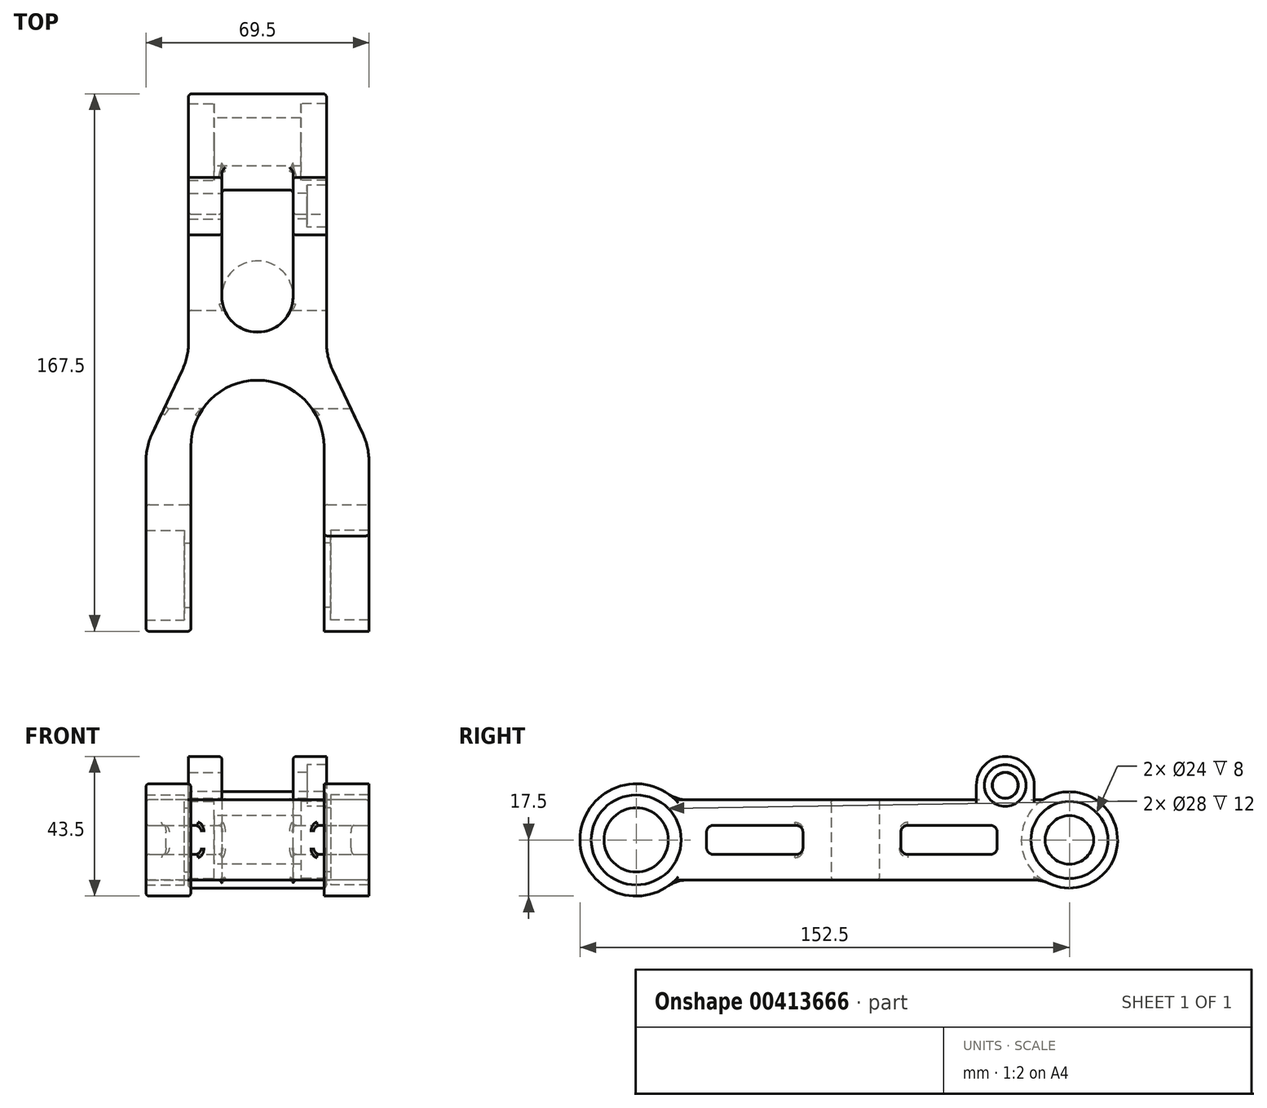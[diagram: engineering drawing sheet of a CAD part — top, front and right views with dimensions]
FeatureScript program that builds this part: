
annotation { "Feature Type Name" : "Feature", "Feature Type Description" : "" }
export const myFeature = defineFeature(function(context is Context, id is Id, definition is map)
    precondition{}
    {
        {
            var Q0;
            Q0=qCreatedBy(makeId("Top.planeOp"),FACE);
            var sketch = newSketch(context, id + "F0", { "sketchPlane" : qUnion([Q0])});
            skLineSegment(sketch, "E0", {"start": v(-21.5, 135) * mm, "end": v(-21.5, 68) * mm});
            skLineSegment(sketch, "E1", {"start": v(-21.5, 68) * mm, "end": v(-34.75, 40) * mm});
            skLineSegment(sketch, "E2", {"start": v(-34.75, 40) * mm, "end": v(-34.75, 0) * mm});
            skLineSegment(sketch, "E3", {"start": v(-34.75, 0) * mm, "end": v(-20.75, 0) * mm});
            skLineSegment(sketch, "E4", {"start": v(-20.75, 0) * mm, "end": v(-20.75, 40) * mm});
            skLineSegment(sketch, "E5", {"start": v(20.75, 0) * mm, "end": v(20.75, 40) * mm});
            skLineSegment(sketch, "E6", {"start": v(20.75, 0) * mm, "end": v(34.75, 0) * mm});
            skLineSegment(sketch, "E7", {"start": v(34.75, 0) * mm, "end": v(34.75, 40) * mm});
            skLineSegment(sketch, "E8", {"start": v(34.75, 40) * mm, "end": v(21.5, 68) * mm});
            skLineSegment(sketch, "E9", {"start": v(21.5, 68) * mm, "end": v(21.5, 135) * mm});
            skLineSegment(sketch, "E10", {"start": v(11.1, 135) * mm, "end": v(21.5, 135) * mm});
            skLineSegment(sketch, "E11", {"start": v(0, 0) * mm, "end": v(0, 68) * mm, "construction": true});
            skLineSegment(sketch, "E12", {"start": v(-11.1, 135) * mm, "end": v(-11.1, 86.85) * mm});
            skLineSegment(sketch, "E13", {"start": v(11.1, 86.85) * mm, "end": v(11.1, 135) * mm});
            skPoint(sketch, "E14.orphan", {"position": v(0, 135) * mm});
            skLineSegment(sketch, "E15", {"start": v(-34.75, 40) * mm, "end": v(34.75, 40) * mm, "construction": true});
            skArc(sketch, "E16", {"start": v(20.75, 40) * mm, "mid": v(0, 60.75) * mm, "end": v(-20.75, 40) * mm});
            skLineSegment(sketch, "E17", {"start": v(-21.5, 135) * mm, "end": v(-11.1, 135) * mm});
            skArc(sketch, "E18", {"start": v(-11.1, 86.85) * mm, "mid": v(0, 75.75) * mm, "end": v(11.1, 86.85) * mm});
            skLineSegment(sketch, "E19", {"start": v(-21.5, 68) * mm, "end": v(21.5, 68) * mm, "construction": true});
            skSolve(sketch);
        }
        {
            var Q0;
            Q0=makeQuery(id+"F0.imprint","IMPRINT",FACE,{"disambiguationData":[TD([[makeQuery(id+"F0.imprint","IMPRINT",EDGE,{"derivedFrom":sQuery(id+"F0.wireOp",EDGE,"E0")}),1.0]])]});
            extrude(context, id + "F1", {"entities" : qUnion([Q0]), "depth" : 25 * mm, "offsetDistance" : 25 * mm, "symmetric" : true});
        }
        {
            var Q0;
            Q0=makeQuery(id+"F1.opExtrude","SWEPT_FACE",FACE,{"disambiguationData":[OSD([sQuery(id+"F0.wireOp",EDGE,"E0")])]});
            var sketch = newSketch(context, id + "F2", { "sketchPlane" : qUnion([Q0])});
            skCircle(sketch, "E20", {"center": v(-135, 0) * mm, "radius": 15 * mm});
            skSolve(sketch);
        }
        {
            var Q0;
            Q0 = qSketchRegion(id + "F2", true);
            var Q1;
            Q1=makeQuery(id+"F1.opExtrude","SWEPT_FACE",FACE,{"disambiguationData":[OSD([sQuery(id+"F0.wireOp",EDGE,"E9")])]});
            extrude(context, id + "F3", {"entities" : qUnion([Q0]), "operationType" : NewBodyOperationType.ADD, "endBound" : BoundingType.UP_TO_SURFACE, "oppositeDirection" : true, "endBoundEntityFace" : qUnion([Q1]), "depth" : 25 * mm});
        }
        {
            var Q0;
            Q0=makeQuery(id+"F1.opExtrude","SWEPT_FACE",FACE,{"disambiguationData":[OSD([sQuery(id+"F0.wireOp",EDGE,"E4")])]});
            var sketch = newSketch(context, id + "F4", { "sketchPlane" : qUnion([Q0])});
            skCircle(sketch, "E21", {"center": v(0, 0) * mm, "radius": 17.5 * mm});
            skSolve(sketch);
        }
        {
            var Q0;
            Q0 = qSketchRegion(id + "F4", true);
            var Q1;
            Q1=makeQuery(id+"F1.opExtrude","SWEPT_FACE",FACE,{"disambiguationData":[OSD([sQuery(id+"F0.wireOp",EDGE,"E2")])]});
            extrude(context, id + "F5", {"entities" : qUnion([Q0]), "operationType" : NewBodyOperationType.ADD, "endBound" : BoundingType.UP_TO_SURFACE, "oppositeDirection" : true, "endBoundEntityFace" : qUnion([Q1]), "depth" : 25 * mm});
        }
        {
            var Q0;
            Q0=makeQuery(id+"F1.opExtrude","SWEPT_FACE",FACE,{"disambiguationData":[OSD([sQuery(id+"F0.wireOp",EDGE,"E5")])]});
            var sketch = newSketch(context, id + "F6", { "sketchPlane" : qUnion([Q0])});
            skCircle(sketch, "E22", {"center": v(0, 0) * mm, "radius": 17.5 * mm});
            skSolve(sketch);
        }
        {
            var Q0;
            {var subQ1=sQuery(id+"F0.wireOp",EDGE,"E5");var subQ6=makeQuery(id+"F1.opExtrude","SWEPT_EDGE",EDGE,{"disambiguationData":[OSD([subQ1,sQuery(id+"F0.wireOp",EDGE,"E6")])]});Q0=makeQuery(id+"F6.imprint","IMPRINT",FACE,{"disambiguationData":[TD([[makeQuery(id+"F6.imprint","IMPRINT",EDGE,{"derivedFrom":subQ6}),1.0]])]});}
            var Q1;
            Q1=makeQuery(id+"F1.opExtrude","SWEPT_FACE",FACE,{"disambiguationData":[OSD([sQuery(id+"F0.wireOp",EDGE,"E7")])]});
            extrude(context, id + "F7", {"entities" : qUnion([Q0]), "operationType" : NewBodyOperationType.ADD, "endBound" : BoundingType.UP_TO_SURFACE, "oppositeDirection" : true, "endBoundEntityFace" : qUnion([Q1]), "depth" : 25 * mm});
        }
        {
            var Q0;
            Q0=qCreatedBy(makeId("Right.planeOp"),FACE);
            var sketch = newSketch(context, id + "F8", { "sketchPlane" : qUnion([Q0])});
            skArc(sketch, "E23", {"start": v(124, 17) * mm, "mid": v(115, 26) * mm, "end": v(106, 17) * mm});
            skLineSegment(sketch, "E24", {"start": v(106, 17) * mm, "end": v(106, 12.5) * mm});
            skLineSegment(sketch, "E25", {"start": v(124, 17) * mm, "end": v(124, 12.5) * mm});
            skLineSegment(sketch, "E26", {"start": v(106, 17) * mm, "end": v(124, 17) * mm, "construction": true});
            skLineSegment(sketch, "E27", {"start": v(106, 12.5) * mm, "end": v(124, 12.5) * mm});
            skSolve(sketch);
        }
        {
            var Q0;
            Q0=makeQuery(id+"F8.imprint","IMPRINT",FACE,{"disambiguationData":[TD([[makeQuery(id+"F8.imprint","IMPRINT",EDGE,{"derivedFrom":sQuery(id+"F8.wireOp",EDGE,"E23")}),1.0]])]});
            var Q1;
            Q1=sQuery(id+"F8.wireOp",EDGE,"E23");
            var Q2;
            Q2=makeQuery(id+"F3.boolean.opBoolean","MERGE",FACE,{"derivedFrom":[makeQuery(id+"F1.opExtrude","SWEPT_FACE",FACE,{"disambiguationData":[OSD([sQuery(id+"F0.wireOp",EDGE,"E9")])]}),makeQuery(id+"F3.opExtrude","CAP_FACE",FACE,{"disambiguationData":[OSD([sQuery(id+"F2.wireOp",EDGE,"E20")])],"isStart":false})]});
            var Q3;
            Q3=makeQuery(id+"F1.opExtrude","SWEPT_FACE",FACE,{"disambiguationData":[OSD([sQuery(id+"F0.wireOp",EDGE,"E13")])]});
            extrude(context, id + "F9", {"entities" : qUnion([Q0]), "operationType" : NewBodyOperationType.ADD, "surfaceEntities" : qUnion([Q1]), "endBound" : BoundingType.UP_TO_SURFACE, "endBoundEntityFace" : qUnion([Q2]), "depth" : 45 * mm, "hasSecondDirection" : true, "secondDirectionBound" : BoundingType.UP_TO_SURFACE, "secondDirectionOppositeDirection" : false, "secondDirectionBoundEntityFace" : qUnion([Q3]), "secondDirectionDepth" : (45 / 2) * mm});
        }
        {
            var Q0;
            Q0 = qSketchRegion(id + "F8", true);
            var Q1;
            Q1=makeQuery(id+"F3.boolean.opBoolean","MERGE",FACE,{"derivedFrom":[makeQuery(id+"F1.opExtrude","SWEPT_FACE",FACE,{"disambiguationData":[OSD([sQuery(id+"F0.wireOp",EDGE,"E0")])]}),makeQuery(id+"F3.opExtrude","CAP_FACE",FACE,{"disambiguationData":[OSD([sQuery(id+"F2.wireOp",EDGE,"E20")])],"isStart":true})]});
            var Q2;
            Q2=makeQuery(id+"F1.opExtrude","SWEPT_FACE",FACE,{"disambiguationData":[OSD([sQuery(id+"F0.wireOp",EDGE,"E12")])]});
            extrude(context, id + "F10", {"entities" : qUnion([Q0]), "operationType" : NewBodyOperationType.ADD, "endBound" : BoundingType.UP_TO_SURFACE, "oppositeDirection" : true, "endBoundEntityFace" : qUnion([Q1]), "depth" : 25 * mm, "hasSecondDirection" : true, "secondDirectionBound" : BoundingType.UP_TO_SURFACE, "secondDirectionOppositeDirection" : true, "secondDirectionBoundEntityFace" : qUnion([Q2]), "secondDirectionDepth" : 25 * mm});
        }
        {
            var Q0;
            Q0=makeQuery(id+"F1.opExtrude","SWEPT_EDGE",EDGE,{"disambiguationData":[OSD([sQuery(id+"F0.wireOp",EDGE,"E0"),sQuery(id+"F0.wireOp",EDGE,"E1")])]});
            var Q1;
            Q1=makeQuery(id+"F1.opExtrude","SWEPT_EDGE",EDGE,{"disambiguationData":[OSD([sQuery(id+"F0.wireOp",EDGE,"E1"),sQuery(id+"F0.wireOp",EDGE,"E2")])]});
            var Q2;
            Q2=makeQuery(id+"F1.opExtrude","SWEPT_EDGE",EDGE,{"disambiguationData":[OSD([sQuery(id+"F0.wireOp",EDGE,"E8"),sQuery(id+"F0.wireOp",EDGE,"E9")])]});
            var Q3;
            Q3=makeQuery(id+"F1.opExtrude","SWEPT_EDGE",EDGE,{"disambiguationData":[OSD([sQuery(id+"F0.wireOp",EDGE,"E7"),sQuery(id+"F0.wireOp",EDGE,"E8")])]});
            fillet(context, id + "F11", {"entities" : qUnion([Q0, Q1, Q2, Q3]), "radius" : 20 * mm, "tangentPropagation" : true, "allowEdgeOverflow" : false});
        }
        {
            var Q0;
            Q0=makeQuery(id+"F9.opExtrude","TWEAK_EDGE",EDGE,{"derivedFrom":[makeQuery(id+"F8.imprint","IMPRINT",EDGE,{"derivedFrom":sQuery(id+"F8.wireOp",EDGE,"E24")}),makeQuery(id+"F8.imprint","IMPRINT",EDGE,{"derivedFrom":sQuery(id+"F8.wireOp",EDGE,"E27")})]});
            var Q1;
            Q1=makeQuery(id+"F10.opExtrude","TWEAK_EDGE",EDGE,{"derivedFrom":[makeQuery(id+"F8.imprint","IMPRINT",EDGE,{"derivedFrom":sQuery(id+"F8.wireOp",EDGE,"E24")}),makeQuery(id+"F8.imprint","IMPRINT",EDGE,{"derivedFrom":sQuery(id+"F8.wireOp",EDGE,"E27")})]});
            var Q2;
            Q2=makeQuery(id+"F9.boolean.opBoolean","INTERSECT",EDGE,{"derivedFrom":[makeQuery(id+"F3.opExtrude","SWEPT_FACE",FACE,{"disambiguationData":[OSD([sQuery(id+"F2.wireOp",EDGE,"E20")])]}),makeQuery(id+"F9.opExtrude","SWEPT_FACE",FACE,{"disambiguationData":[OSD([sQuery(id+"F8.wireOp",EDGE,"E25")])]})]});
            var Q3;
            Q3=makeQuery(id+"F10.boolean.opBoolean","INTERSECT",EDGE,{"derivedFrom":[makeQuery(id+"F3.opExtrude","SWEPT_FACE",FACE,{"disambiguationData":[OSD([sQuery(id+"F2.wireOp",EDGE,"E20")])]}),makeQuery(id+"F10.opExtrude","SWEPT_FACE",FACE,{"disambiguationData":[OSD([sQuery(id+"F8.wireOp",EDGE,"E25")])]})]});
            var Q4;
            {var subQ0=sQuery(id+"F6.wireOp",EDGE,"E22");var subQ1=sQuery(id+"F0.wireOp",EDGE,"E5");Q4=makeQuery(id+"F7.opExtrude","SWEPT_EDGE",EDGE,{"disambiguationData":[OSD([subQ1,subQ0]),TDD([makeQuery(id+"F6.imprint","INTERSECT",VERTEX,{"derivedFrom":[makeQuery(id+"F1.opExtrude","CAP_EDGE",EDGE,{"disambiguationData":[OSD([subQ1])],"isStart":false}),subQ0]})])]});}
            var Q5;
            Q5=makeQuery(id+"F5.boolean.opBoolean","INTERSECT",EDGE,{"derivedFrom":[makeQuery(id+"F1.opExtrude","CAP_FACE",FACE,{"disambiguationData":[OSD([sQuery(id+"F0.wireOp",EDGE,"E0"),sQuery(id+"F0.wireOp",EDGE,"E1"),sQuery(id+"F0.wireOp",EDGE,"E2"),sQuery(id+"F0.wireOp",EDGE,"E3"),sQuery(id+"F0.wireOp",EDGE,"E4"),sQuery(id+"F0.wireOp",EDGE,"E5"),sQuery(id+"F0.wireOp",EDGE,"E6"),sQuery(id+"F0.wireOp",EDGE,"E7"),sQuery(id+"F0.wireOp",EDGE,"E8"),sQuery(id+"F0.wireOp",EDGE,"E9"),sQuery(id+"F0.wireOp",EDGE,"E10"),sQuery(id+"F0.wireOp",EDGE,"E12"),sQuery(id+"F0.wireOp",EDGE,"E13"),sQuery(id+"F0.wireOp",EDGE,"E16"),sQuery(id+"F0.wireOp",EDGE,"E17"),sQuery(id+"F0.wireOp",EDGE,"E18")])],"isStart":false}),makeQuery(id+"F5.opExtrude","SWEPT_FACE",FACE,{"disambiguationData":[OSD([sQuery(id+"F4.wireOp",EDGE,"E21")])]})]});
            var Q6;
            {var subQ0=sQuery(id+"F6.wireOp",EDGE,"E22");var subQ1=sQuery(id+"F0.wireOp",EDGE,"E5");Q6=makeQuery(id+"F7.opExtrude","SWEPT_EDGE",EDGE,{"disambiguationData":[OSD([subQ1,subQ0]),TDD([makeQuery(id+"F6.imprint","INTERSECT",VERTEX,{"derivedFrom":[makeQuery(id+"F1.opExtrude","CAP_EDGE",EDGE,{"disambiguationData":[OSD([subQ1])],"isStart":true}),subQ0]})])]});}
            var Q7;
            Q7=makeQuery(id+"F5.boolean.opBoolean","INTERSECT",EDGE,{"derivedFrom":[makeQuery(id+"F1.opExtrude","CAP_FACE",FACE,{"disambiguationData":[OSD([sQuery(id+"F0.wireOp",EDGE,"E0"),sQuery(id+"F0.wireOp",EDGE,"E1"),sQuery(id+"F0.wireOp",EDGE,"E2"),sQuery(id+"F0.wireOp",EDGE,"E3"),sQuery(id+"F0.wireOp",EDGE,"E4"),sQuery(id+"F0.wireOp",EDGE,"E5"),sQuery(id+"F0.wireOp",EDGE,"E6"),sQuery(id+"F0.wireOp",EDGE,"E7"),sQuery(id+"F0.wireOp",EDGE,"E8"),sQuery(id+"F0.wireOp",EDGE,"E9"),sQuery(id+"F0.wireOp",EDGE,"E10"),sQuery(id+"F0.wireOp",EDGE,"E12"),sQuery(id+"F0.wireOp",EDGE,"E13"),sQuery(id+"F0.wireOp",EDGE,"E16"),sQuery(id+"F0.wireOp",EDGE,"E17"),sQuery(id+"F0.wireOp",EDGE,"E18")])],"isStart":true}),makeQuery(id+"F5.opExtrude","SWEPT_FACE",FACE,{"disambiguationData":[OSD([sQuery(id+"F4.wireOp",EDGE,"E21")])]})]});
            var Q8;
            Q8=makeQuery(id+"F3.boolean.opBoolean","INTERSECT",EDGE,{"disambiguationData":[OD(1.0)],"derivedFrom":[makeQuery(id+"F1.opExtrude","CAP_FACE",FACE,{"disambiguationData":[OSD([sQuery(id+"F0.wireOp",EDGE,"E0"),sQuery(id+"F0.wireOp",EDGE,"E1"),sQuery(id+"F0.wireOp",EDGE,"E2"),sQuery(id+"F0.wireOp",EDGE,"E3"),sQuery(id+"F0.wireOp",EDGE,"E4"),sQuery(id+"F0.wireOp",EDGE,"E5"),sQuery(id+"F0.wireOp",EDGE,"E6"),sQuery(id+"F0.wireOp",EDGE,"E7"),sQuery(id+"F0.wireOp",EDGE,"E8"),sQuery(id+"F0.wireOp",EDGE,"E9"),sQuery(id+"F0.wireOp",EDGE,"E10"),sQuery(id+"F0.wireOp",EDGE,"E12"),sQuery(id+"F0.wireOp",EDGE,"E13"),sQuery(id+"F0.wireOp",EDGE,"E16"),sQuery(id+"F0.wireOp",EDGE,"E17"),sQuery(id+"F0.wireOp",EDGE,"E18")])],"isStart":true}),makeQuery(id+"F3.opExtrude","SWEPT_FACE",FACE,{"disambiguationData":[OSD([sQuery(id+"F2.wireOp",EDGE,"E20")])]})]});
            var Q9;
            Q9=makeQuery(id+"F3.boolean.opBoolean","INTERSECT",EDGE,{"disambiguationData":[OD(0.0)],"derivedFrom":[makeQuery(id+"F1.opExtrude","CAP_FACE",FACE,{"disambiguationData":[OSD([sQuery(id+"F0.wireOp",EDGE,"E0"),sQuery(id+"F0.wireOp",EDGE,"E1"),sQuery(id+"F0.wireOp",EDGE,"E2"),sQuery(id+"F0.wireOp",EDGE,"E3"),sQuery(id+"F0.wireOp",EDGE,"E4"),sQuery(id+"F0.wireOp",EDGE,"E5"),sQuery(id+"F0.wireOp",EDGE,"E6"),sQuery(id+"F0.wireOp",EDGE,"E7"),sQuery(id+"F0.wireOp",EDGE,"E8"),sQuery(id+"F0.wireOp",EDGE,"E9"),sQuery(id+"F0.wireOp",EDGE,"E10"),sQuery(id+"F0.wireOp",EDGE,"E12"),sQuery(id+"F0.wireOp",EDGE,"E13"),sQuery(id+"F0.wireOp",EDGE,"E16"),sQuery(id+"F0.wireOp",EDGE,"E17"),sQuery(id+"F0.wireOp",EDGE,"E18")])],"isStart":true}),makeQuery(id+"F3.opExtrude","SWEPT_FACE",FACE,{"disambiguationData":[OSD([sQuery(id+"F2.wireOp",EDGE,"E20")])]})]});
            fillet(context, id + "F12", {"entities" : qUnion([Q0, Q1, Q2, Q3, Q4, Q5, Q6, Q7, Q8, Q9]), "radius" : 10 * mm, "allowEdgeOverflow" : false});
        }
        {
            var Q0;
            Q0=makeQuery(id+"F3.boolean.opBoolean","INTERSECT",EDGE,{"disambiguationData":[OD(1.0)],"derivedFrom":[makeQuery(id+"F1.opExtrude","CAP_FACE",FACE,{"disambiguationData":[OSD([sQuery(id+"F0.wireOp",EDGE,"E0"),sQuery(id+"F0.wireOp",EDGE,"E1"),sQuery(id+"F0.wireOp",EDGE,"E2"),sQuery(id+"F0.wireOp",EDGE,"E3"),sQuery(id+"F0.wireOp",EDGE,"E4"),sQuery(id+"F0.wireOp",EDGE,"E5"),sQuery(id+"F0.wireOp",EDGE,"E6"),sQuery(id+"F0.wireOp",EDGE,"E7"),sQuery(id+"F0.wireOp",EDGE,"E8"),sQuery(id+"F0.wireOp",EDGE,"E9"),sQuery(id+"F0.wireOp",EDGE,"E10"),sQuery(id+"F0.wireOp",EDGE,"E12"),sQuery(id+"F0.wireOp",EDGE,"E13"),sQuery(id+"F0.wireOp",EDGE,"E16"),sQuery(id+"F0.wireOp",EDGE,"E17"),sQuery(id+"F0.wireOp",EDGE,"E18")])],"isStart":false}),makeQuery(id+"F3.opExtrude","SWEPT_FACE",FACE,{"disambiguationData":[OSD([sQuery(id+"F2.wireOp",EDGE,"E20")])]})]});
            var Q1;
            Q1=makeQuery(id+"F9.opExtrude","TWEAK_EDGE",EDGE,{"derivedFrom":[makeQuery(id+"F8.imprint","IMPRINT",EDGE,{"derivedFrom":sQuery(id+"F8.wireOp",EDGE,"E25")}),makeQuery(id+"F8.imprint","IMPRINT",EDGE,{"derivedFrom":sQuery(id+"F8.wireOp",EDGE,"E27")})]});
            var Q2;
            Q2=makeQuery(id+"F10.opExtrude","TWEAK_EDGE",EDGE,{"derivedFrom":[makeQuery(id+"F8.imprint","IMPRINT",EDGE,{"derivedFrom":sQuery(id+"F8.wireOp",EDGE,"E25")}),makeQuery(id+"F8.imprint","IMPRINT",EDGE,{"derivedFrom":sQuery(id+"F8.wireOp",EDGE,"E27")})]});
            var Q3;
            Q3=makeQuery(id+"F3.boolean.opBoolean","INTERSECT",EDGE,{"disambiguationData":[OD(0.0)],"derivedFrom":[makeQuery(id+"F1.opExtrude","CAP_FACE",FACE,{"disambiguationData":[OSD([sQuery(id+"F0.wireOp",EDGE,"E0"),sQuery(id+"F0.wireOp",EDGE,"E1"),sQuery(id+"F0.wireOp",EDGE,"E2"),sQuery(id+"F0.wireOp",EDGE,"E3"),sQuery(id+"F0.wireOp",EDGE,"E4"),sQuery(id+"F0.wireOp",EDGE,"E5"),sQuery(id+"F0.wireOp",EDGE,"E6"),sQuery(id+"F0.wireOp",EDGE,"E7"),sQuery(id+"F0.wireOp",EDGE,"E8"),sQuery(id+"F0.wireOp",EDGE,"E9"),sQuery(id+"F0.wireOp",EDGE,"E10"),sQuery(id+"F0.wireOp",EDGE,"E12"),sQuery(id+"F0.wireOp",EDGE,"E13"),sQuery(id+"F0.wireOp",EDGE,"E16"),sQuery(id+"F0.wireOp",EDGE,"E17"),sQuery(id+"F0.wireOp",EDGE,"E18")])],"isStart":false}),makeQuery(id+"F3.opExtrude","SWEPT_FACE",FACE,{"disambiguationData":[OSD([sQuery(id+"F2.wireOp",EDGE,"E20")])]})]});
            var Q4;
            Q4=makeQuery(id+"F3.boolean.opBoolean","INTERSECT",EDGE,{"derivedFrom":[makeQuery(id+"F1.opExtrude","SWEPT_FACE",FACE,{"disambiguationData":[OSD([sQuery(id+"F0.wireOp",EDGE,"E13")])]}),makeQuery(id+"F3.opExtrude","SWEPT_FACE",FACE,{"disambiguationData":[OSD([sQuery(id+"F2.wireOp",EDGE,"E20")])]})]});
            var Q5;
            Q5=makeQuery(id+"F3.boolean.opBoolean","INTERSECT",EDGE,{"derivedFrom":[makeQuery(id+"F1.opExtrude","SWEPT_FACE",FACE,{"disambiguationData":[OSD([sQuery(id+"F0.wireOp",EDGE,"E12")])]}),makeQuery(id+"F3.opExtrude","SWEPT_FACE",FACE,{"disambiguationData":[OSD([sQuery(id+"F2.wireOp",EDGE,"E20")])]})]});
            fillet(context, id + "F13", {"entities" : qUnion([Q0, Q1, Q2, Q3, Q4, Q5]), "radius" : 1 * mm, "tangentPropagation" : true, "allowEdgeOverflow" : false});
        }
        {
            var Q0;
            Q0=makeQuery(id+"F10.opExtrude","CAP_EDGE",EDGE,{"disambiguationData":[OSD([sQuery(id+"F8.wireOp",EDGE,"E23")])],"isStart":true});
            var Q1;
            Q1=makeQuery(id+"F9.opExtrude","CAP_EDGE",EDGE,{"disambiguationData":[OSD([sQuery(id+"F8.wireOp",EDGE,"E23")])],"isStart":true});
            fillet(context, id + "F14", {"entities" : qUnion([Q0, Q1]), "radius" : 1 * mm, "tangentPropagation" : true, "allowEdgeOverflow" : false});
        }
        {
            var Q0;
            Q0=makeQuery(id+"F1.opExtrude","CAP_EDGE",EDGE,{"disambiguationData":[OSD([sQuery(id+"F0.wireOp",EDGE,"E13")])],"isStart":true});
            var Q1;
            Q1=makeQuery(id+"F1.opExtrude","CAP_EDGE",EDGE,{"disambiguationData":[OSD([sQuery(id+"F0.wireOp",EDGE,"E12")])],"isStart":true});
            fillet(context, id + "F15", {"entities" : qUnion([Q0, Q1]), "radius" : 1 * mm, "tangentPropagation" : true, "allowEdgeOverflow" : false});
        }
        {
            var Q0;
            Q0=makeQuery(id+"F1.opExtrude","CAP_EDGE",EDGE,{"disambiguationData":[OSD([sQuery(id+"F0.wireOp",EDGE,"E5")])],"isStart":true});
            fillet(context, id + "F16", {"entities" : qUnion([Q0]), "radius" : 1 * mm, "tangentPropagation" : true, "allowEdgeOverflow" : false});
        }
        {
            var Q0;
            Q0=makeQuery(id+"F1.opExtrude","CAP_EDGE",EDGE,{"disambiguationData":[OSD([sQuery(id+"F0.wireOp",EDGE,"E9")])],"isStart":false});
            var Q1;
            Q1=makeQuery(id+"F1.opExtrude","CAP_EDGE",EDGE,{"disambiguationData":[OSD([sQuery(id+"F0.wireOp",EDGE,"E0")])],"isStart":false});
            fillet(context, id + "F17", {"entities" : qUnion([Q0, Q1]), "radius" : 1 * mm, "tangentPropagation" : true, "allowEdgeOverflow" : false});
        }
        {
            var Q0;
            Q0=makeQuery(id+"F9.boolean.opBoolean","MERGE",FACE,{"derivedFrom":[makeQuery(id+"F3.boolean.opBoolean","MERGE",FACE,{"derivedFrom":[makeQuery(id+"F1.opExtrude","SWEPT_FACE",FACE,{"disambiguationData":[OSD([sQuery(id+"F0.wireOp",EDGE,"E9")])]}),makeQuery(id+"F3.opExtrude","CAP_FACE",FACE,{"disambiguationData":[OSD([sQuery(id+"F2.wireOp",EDGE,"E20")])],"isStart":false})]}),makeQuery(id+"F9.opExtrude","CAP_FACE",FACE,{"disambiguationData":[OSD([sQuery(id+"F8.wireOp",EDGE,"E23"),sQuery(id+"F8.wireOp",EDGE,"E24"),sQuery(id+"F8.wireOp",EDGE,"E25"),sQuery(id+"F8.wireOp",EDGE,"E27")])],"isStart":false})]});
            var sketch = newSketch(context, id + "F18", { "sketchPlane" : qUnion([Q0])});
            skPoint(sketch, "E28", {"position": v(115, 17) * mm});
            skSolve(sketch);
        }
        {
            var Q0;
            Q0=sQuery(id+"F18.wireOp",VERTEX,"E28");
            var Q1;
            Q1=makeQuery(id+"F1.opExtrude","SWEPT_BODY",BODY,{"disambiguationData":[OSD([sQuery(id+"F0.wireOp",EDGE,"E0"),sQuery(id+"F0.wireOp",EDGE,"E1"),sQuery(id+"F0.wireOp",EDGE,"E2"),sQuery(id+"F0.wireOp",EDGE,"E3"),sQuery(id+"F0.wireOp",EDGE,"E4"),sQuery(id+"F0.wireOp",EDGE,"E5"),sQuery(id+"F0.wireOp",EDGE,"E6"),sQuery(id+"F0.wireOp",EDGE,"E7"),sQuery(id+"F0.wireOp",EDGE,"E8"),sQuery(id+"F0.wireOp",EDGE,"E9"),sQuery(id+"F0.wireOp",EDGE,"E10"),sQuery(id+"F0.wireOp",EDGE,"E12"),sQuery(id+"F0.wireOp",EDGE,"E13"),sQuery(id+"F0.wireOp",EDGE,"E16"),sQuery(id+"F0.wireOp",EDGE,"E17"),sQuery(id+"F0.wireOp",EDGE,"E18")])]});
            hole(context, id + "F19", {"style" : HoleStyle.C_BORE, "endStyle" : HoleEndStyle.BLIND, "holeDiameter" : 8.1 * mm, "cBoreDiameter" : 13 * mm, "cBoreDepth" : 6 * mm, "majorDiameter" : 5 * mm, "holeDepth" : 12 * mm, "isTappedThrough" : true, "tappedDepth" : 12 * mm, "tapClearance" : 3, "locations" : qUnion([Q0]), "scope" : qUnion([Q1]), "startStyle" : HoleStartStyle.SKETCH});
        }
        {
            var Q0;
            Q0=makeQuery(id+"F10.boolean.opBoolean","MERGE",FACE,{"derivedFrom":[makeQuery(id+"F3.boolean.opBoolean","MERGE",FACE,{"derivedFrom":[makeQuery(id+"F1.opExtrude","SWEPT_FACE",FACE,{"disambiguationData":[OSD([sQuery(id+"F0.wireOp",EDGE,"E0")])]}),makeQuery(id+"F3.opExtrude","CAP_FACE",FACE,{"disambiguationData":[OSD([sQuery(id+"F2.wireOp",EDGE,"E20")])],"isStart":true})]}),makeQuery(id+"F10.opExtrude","CAP_FACE",FACE,{"disambiguationData":[OSD([sQuery(id+"F8.wireOp",EDGE,"E23"),sQuery(id+"F8.wireOp",EDGE,"E24"),sQuery(id+"F8.wireOp",EDGE,"E25"),sQuery(id+"F8.wireOp",EDGE,"E27")])],"isStart":false})]});
            var sketch = newSketch(context, id + "F20", { "sketchPlane" : qUnion([Q0])});
            skPoint(sketch, "E29", {"position": v(-115, 17) * mm});
            skSolve(sketch);
        }
        {
            var Q0;
            Q0=sQuery(id+"F20.wireOp",VERTEX,"E29");
            var Q1;
            Q1=makeQuery(id+"F1.opExtrude","SWEPT_BODY",BODY,{"disambiguationData":[OSD([sQuery(id+"F0.wireOp",EDGE,"E0"),sQuery(id+"F0.wireOp",EDGE,"E1"),sQuery(id+"F0.wireOp",EDGE,"E2"),sQuery(id+"F0.wireOp",EDGE,"E3"),sQuery(id+"F0.wireOp",EDGE,"E4"),sQuery(id+"F0.wireOp",EDGE,"E5"),sQuery(id+"F0.wireOp",EDGE,"E6"),sQuery(id+"F0.wireOp",EDGE,"E7"),sQuery(id+"F0.wireOp",EDGE,"E8"),sQuery(id+"F0.wireOp",EDGE,"E9"),sQuery(id+"F0.wireOp",EDGE,"E10"),sQuery(id+"F0.wireOp",EDGE,"E12"),sQuery(id+"F0.wireOp",EDGE,"E13"),sQuery(id+"F0.wireOp",EDGE,"E16"),sQuery(id+"F0.wireOp",EDGE,"E17"),sQuery(id+"F0.wireOp",EDGE,"E18")])]});
            hole(context, id + "F21", {"style" : HoleStyle.SIMPLE, "endStyle" : HoleEndStyle.BLIND, "holeDiameter" : 8 * mm, "holeDepth" : 15.75 * mm, "isTappedThrough" : true, "tappedDepth" : 12 * mm, "tapClearance" : 3, "locations" : qUnion([Q0]), "scope" : qUnion([Q1]), "startStyle" : HoleStartStyle.SKETCH});
        }
        {
            var Q0;
            Q0=makeQuery(id+"F9.boolean.opBoolean","MERGE",FACE,{"derivedFrom":[makeQuery(id+"F3.boolean.opBoolean","MERGE",FACE,{"derivedFrom":[makeQuery(id+"F1.opExtrude","SWEPT_FACE",FACE,{"disambiguationData":[OSD([sQuery(id+"F0.wireOp",EDGE,"E9")])]}),makeQuery(id+"F3.opExtrude","CAP_FACE",FACE,{"disambiguationData":[OSD([sQuery(id+"F2.wireOp",EDGE,"E20")])],"isStart":false})]}),makeQuery(id+"F9.opExtrude","CAP_FACE",FACE,{"disambiguationData":[OSD([sQuery(id+"F8.wireOp",EDGE,"E23"),sQuery(id+"F8.wireOp",EDGE,"E24"),sQuery(id+"F8.wireOp",EDGE,"E25"),sQuery(id+"F8.wireOp",EDGE,"E27")])],"isStart":false})]});
            var sketch = newSketch(context, id + "F22", { "sketchPlane" : qUnion([Q0])});
            skPoint(sketch, "E30", {"position": v(135, 0) * mm});
            skSolve(sketch);
        }
        {
            var Q0;
            Q0=sQuery(id+"F22.wireOp",VERTEX,"E30");
            var Q1;
            Q1=makeQuery(id+"F1.opExtrude","SWEPT_BODY",BODY,{"disambiguationData":[OSD([sQuery(id+"F0.wireOp",EDGE,"E0"),sQuery(id+"F0.wireOp",EDGE,"E1"),sQuery(id+"F0.wireOp",EDGE,"E2"),sQuery(id+"F0.wireOp",EDGE,"E3"),sQuery(id+"F0.wireOp",EDGE,"E4"),sQuery(id+"F0.wireOp",EDGE,"E5"),sQuery(id+"F0.wireOp",EDGE,"E6"),sQuery(id+"F0.wireOp",EDGE,"E7"),sQuery(id+"F0.wireOp",EDGE,"E8"),sQuery(id+"F0.wireOp",EDGE,"E9"),sQuery(id+"F0.wireOp",EDGE,"E10"),sQuery(id+"F0.wireOp",EDGE,"E12"),sQuery(id+"F0.wireOp",EDGE,"E13"),sQuery(id+"F0.wireOp",EDGE,"E16"),sQuery(id+"F0.wireOp",EDGE,"E17"),sQuery(id+"F0.wireOp",EDGE,"E18")])]});
            hole(context, id + "F23", {"style" : HoleStyle.C_BORE, "endStyle" : HoleEndStyle.BLIND, "holeDiameter" : 15.1 * mm, "cBoreDiameter" : 24 * mm, "cBoreDepth" : 8 * mm, "majorDiameter" : 5 * mm, "holeDepth" : 30 * mm, "isTappedThrough" : true, "tappedDepth" : 12 * mm, "tapClearance" : 3, "locations" : qUnion([Q0]), "scope" : qUnion([Q1]), "startStyle" : HoleStartStyle.SKETCH});
        }
        {
            var Q0;
            Q0=makeQuery(id+"F10.boolean.opBoolean","MERGE",FACE,{"derivedFrom":[makeQuery(id+"F3.boolean.opBoolean","MERGE",FACE,{"derivedFrom":[makeQuery(id+"F1.opExtrude","SWEPT_FACE",FACE,{"disambiguationData":[OSD([sQuery(id+"F0.wireOp",EDGE,"E0")])]}),makeQuery(id+"F3.opExtrude","CAP_FACE",FACE,{"disambiguationData":[OSD([sQuery(id+"F2.wireOp",EDGE,"E20")])],"isStart":true})]}),makeQuery(id+"F10.opExtrude","CAP_FACE",FACE,{"disambiguationData":[OSD([sQuery(id+"F8.wireOp",EDGE,"E23"),sQuery(id+"F8.wireOp",EDGE,"E24"),sQuery(id+"F8.wireOp",EDGE,"E25"),sQuery(id+"F8.wireOp",EDGE,"E27")])],"isStart":false})]});
            var sketch = newSketch(context, id + "F24", { "sketchPlane" : qUnion([Q0])});
            skPoint(sketch, "E31", {"position": v(-135, 0) * mm});
            skSolve(sketch);
        }
        {
            var Q0;
            Q0=sQuery(id+"F24.wireOp",VERTEX,"E31");
            var Q1;
            Q1=makeQuery(id+"F1.opExtrude","SWEPT_BODY",BODY,{"disambiguationData":[OSD([sQuery(id+"F0.wireOp",EDGE,"E0"),sQuery(id+"F0.wireOp",EDGE,"E1"),sQuery(id+"F0.wireOp",EDGE,"E2"),sQuery(id+"F0.wireOp",EDGE,"E3"),sQuery(id+"F0.wireOp",EDGE,"E4"),sQuery(id+"F0.wireOp",EDGE,"E5"),sQuery(id+"F0.wireOp",EDGE,"E6"),sQuery(id+"F0.wireOp",EDGE,"E7"),sQuery(id+"F0.wireOp",EDGE,"E8"),sQuery(id+"F0.wireOp",EDGE,"E9"),sQuery(id+"F0.wireOp",EDGE,"E10"),sQuery(id+"F0.wireOp",EDGE,"E12"),sQuery(id+"F0.wireOp",EDGE,"E13"),sQuery(id+"F0.wireOp",EDGE,"E16"),sQuery(id+"F0.wireOp",EDGE,"E17"),sQuery(id+"F0.wireOp",EDGE,"E18")])]});
            hole(context, id + "F25", {"style" : HoleStyle.C_BORE, "endStyle" : HoleEndStyle.BLIND, "holeDiameter" : 15.1 * mm, "cBoreDiameter" : 24 * mm, "cBoreDepth" : 8 * mm, "majorDiameter" : 5 * mm, "holeDepth" : 30 * mm, "isTappedThrough" : true, "tappedDepth" : 12 * mm, "tapClearance" : 3, "locations" : qUnion([Q0]), "scope" : qUnion([Q1]), "startStyle" : HoleStartStyle.SKETCH});
        }
        {
            var Q0;
            Q0=makeQuery(id+"F5.boolean.opBoolean","MERGE",FACE,{"derivedFrom":[makeQuery(id+"F1.opExtrude","SWEPT_FACE",FACE,{"disambiguationData":[OSD([sQuery(id+"F0.wireOp",EDGE,"E2")])]}),makeQuery(id+"F5.opExtrude","CAP_FACE",FACE,{"disambiguationData":[OSD([sQuery(id+"F4.wireOp",EDGE,"E21")])],"isStart":false})]});
            var sketch = newSketch(context, id + "F26", { "sketchPlane" : qUnion([Q0])});
            skPoint(sketch, "E32", {"position": v(0, 0) * mm});
            skSolve(sketch);
        }
        {
            var Q0;
            Q0=sQuery(id+"F26.wireOp",VERTEX,"E32");
            var Q1;
            Q1=makeQuery(id+"F1.opExtrude","SWEPT_BODY",BODY,{"disambiguationData":[OSD([sQuery(id+"F0.wireOp",EDGE,"E0"),sQuery(id+"F0.wireOp",EDGE,"E1"),sQuery(id+"F0.wireOp",EDGE,"E2"),sQuery(id+"F0.wireOp",EDGE,"E3"),sQuery(id+"F0.wireOp",EDGE,"E4"),sQuery(id+"F0.wireOp",EDGE,"E5"),sQuery(id+"F0.wireOp",EDGE,"E6"),sQuery(id+"F0.wireOp",EDGE,"E7"),sQuery(id+"F0.wireOp",EDGE,"E8"),sQuery(id+"F0.wireOp",EDGE,"E9"),sQuery(id+"F0.wireOp",EDGE,"E10"),sQuery(id+"F0.wireOp",EDGE,"E12"),sQuery(id+"F0.wireOp",EDGE,"E13"),sQuery(id+"F0.wireOp",EDGE,"E16"),sQuery(id+"F0.wireOp",EDGE,"E17"),sQuery(id+"F0.wireOp",EDGE,"E18")])]});
            hole(context, id + "F27", {"style" : HoleStyle.C_BORE, "endStyle" : HoleEndStyle.BLIND, "holeDiameter" : 20 * mm, "cBoreDiameter" : 28 * mm, "cBoreDepth" : 12 * mm, "majorDiameter" : 5 * mm, "holeDepth" : 30 * mm, "isTappedThrough" : true, "tappedDepth" : 12 * mm, "tapClearance" : 3, "locations" : qUnion([Q0]), "scope" : qUnion([Q1]), "startStyle" : HoleStartStyle.SKETCH});
        }
        {
            var Q0;
            Q0=makeQuery(id+"F7.boolean.opBoolean","MERGE",FACE,{"derivedFrom":[makeQuery(id+"F1.opExtrude","SWEPT_FACE",FACE,{"disambiguationData":[OSD([sQuery(id+"F0.wireOp",EDGE,"E7")])]}),makeQuery(id+"F7.opExtrude","CAP_FACE",FACE,{"disambiguationData":[OSD([sQuery(id+"F0.wireOp",EDGE,"E5"),sQuery(id+"F0.wireOp",EDGE,"E6"),sQuery(id+"F6.wireOp",EDGE,"E22")])],"isStart":false})]});
            var sketch = newSketch(context, id + "F28", { "sketchPlane" : qUnion([Q0])});
            skPoint(sketch, "E33", {"position": v(0, 0) * mm});
            skSolve(sketch);
        }
        {
            var Q0;
            Q0=sQuery(id+"F28.wireOp",VERTEX,"E33");
            var Q1;
            Q1=makeQuery(id+"F1.opExtrude","SWEPT_BODY",BODY,{"disambiguationData":[OSD([sQuery(id+"F0.wireOp",EDGE,"E0"),sQuery(id+"F0.wireOp",EDGE,"E1"),sQuery(id+"F0.wireOp",EDGE,"E2"),sQuery(id+"F0.wireOp",EDGE,"E3"),sQuery(id+"F0.wireOp",EDGE,"E4"),sQuery(id+"F0.wireOp",EDGE,"E5"),sQuery(id+"F0.wireOp",EDGE,"E6"),sQuery(id+"F0.wireOp",EDGE,"E7"),sQuery(id+"F0.wireOp",EDGE,"E8"),sQuery(id+"F0.wireOp",EDGE,"E9"),sQuery(id+"F0.wireOp",EDGE,"E10"),sQuery(id+"F0.wireOp",EDGE,"E12"),sQuery(id+"F0.wireOp",EDGE,"E13"),sQuery(id+"F0.wireOp",EDGE,"E16"),sQuery(id+"F0.wireOp",EDGE,"E17"),sQuery(id+"F0.wireOp",EDGE,"E18")])]});
            hole(context, id + "F29", {"style" : HoleStyle.C_BORE, "endStyle" : HoleEndStyle.BLIND, "holeDiameter" : 20 * mm, "cBoreDiameter" : 28 * mm, "cBoreDepth" : 12 * mm, "majorDiameter" : 5 * mm, "holeDepth" : 30 * mm, "isTappedThrough" : true, "tappedDepth" : 12 * mm, "tapClearance" : 3, "locations" : qUnion([Q0]), "scope" : qUnion([Q1]), "startStyle" : HoleStartStyle.SKETCH});
        }
        {
            var Q0;
            Q0=makeQuery(id+"F9.boolean.opBoolean","MERGE",FACE,{"derivedFrom":[makeQuery(id+"F3.boolean.opBoolean","MERGE",FACE,{"derivedFrom":[makeQuery(id+"F1.opExtrude","SWEPT_FACE",FACE,{"disambiguationData":[OSD([sQuery(id+"F0.wireOp",EDGE,"E9")])]}),makeQuery(id+"F3.opExtrude","CAP_FACE",FACE,{"disambiguationData":[OSD([sQuery(id+"F2.wireOp",EDGE,"E20")])],"isStart":false})]}),makeQuery(id+"F9.opExtrude","CAP_FACE",FACE,{"disambiguationData":[OSD([sQuery(id+"F8.wireOp",EDGE,"E23"),sQuery(id+"F8.wireOp",EDGE,"E24"),sQuery(id+"F8.wireOp",EDGE,"E25"),sQuery(id+"F8.wireOp",EDGE,"E27")])],"isStart":false})]});
            var sketch = newSketch(context, id + "F30", { "sketchPlane" : qUnion([Q0])});
            skLineSegment(sketch, "E34.bottom", {"start": v(84.5, 4.5) * mm, "end": v(110.5, 4.5) * mm});
            skLineSegment(sketch, "E34.top", {"start": v(84.5, -4.5) * mm, "end": v(110.5, -4.5) * mm});
            skLineSegment(sketch, "E34.left", {"start": v(82.5, 2.5) * mm, "end": v(82.5, -2.5) * mm});
            skLineSegment(sketch, "E34.right", {"start": v(112.5, 2.5) * mm, "end": v(112.5, -2.5) * mm});
            skPoint(sketch, "E35.visualSharp", {"position": v(82.5, 4.5) * mm});
            skArc(sketch, "E35.filletArc", {"start": v(84.5, 4.5) * mm, "mid": v(83.08, 3.91) * mm, "end": v(82.5, 2.5) * mm});
            skPoint(sketch, "E36.visualSharp", {"position": v(82.5, -4.5) * mm});
            skArc(sketch, "E36.filletArc", {"start": v(82.5, -2.5) * mm, "mid": v(83.08, -3.91) * mm, "end": v(84.5, -4.5) * mm});
            skPoint(sketch, "E37.visualSharp", {"position": v(112.5, 4.5) * mm});
            skArc(sketch, "E37.filletArc", {"start": v(112.5, 2.5) * mm, "mid": v(111.9, 3.91) * mm, "end": v(110.5, 4.5) * mm});
            skPoint(sketch, "E38.visualSharp", {"position": v(112.5, -4.5) * mm});
            skArc(sketch, "E38.filletArc", {"start": v(110.5, -4.5) * mm, "mid": v(111.9, -3.91) * mm, "end": v(112.5, -2.5) * mm});
            skSolve(sketch);
        }
        {
            var Q0;
            Q0 = qSketchRegion(id + "F30", true);
            extrude(context, id + "F31", {"entities" : qUnion([Q0]), "operationType" : NewBodyOperationType.REMOVE, "endBound" : BoundingType.THROUGH_ALL, "oppositeDirection" : true, "depth" : 25 * mm, "offsetDistance" : 25 * mm});
        }
        {
            var Q0;
            Q0=makeQuery(id+"F31.boolean.opBoolean","INTERSECT",EDGE,{"derivedFrom":[makeQuery(id+"F10.boolean.opBoolean","MERGE",FACE,{"derivedFrom":[makeQuery(id+"F3.boolean.opBoolean","MERGE",FACE,{"derivedFrom":[makeQuery(id+"F1.opExtrude","SWEPT_FACE",FACE,{"disambiguationData":[OSD([sQuery(id+"F0.wireOp",EDGE,"E0")])]}),makeQuery(id+"F3.opExtrude","CAP_FACE",FACE,{"disambiguationData":[OSD([sQuery(id+"F2.wireOp",EDGE,"E20")])],"isStart":true})]}),makeQuery(id+"F10.opExtrude","CAP_FACE",FACE,{"disambiguationData":[OSD([sQuery(id+"F8.wireOp",EDGE,"E23"),sQuery(id+"F8.wireOp",EDGE,"E24"),sQuery(id+"F8.wireOp",EDGE,"E25"),sQuery(id+"F8.wireOp",EDGE,"E27")])],"isStart":false})]}),makeQuery(id+"F31.opExtrude","SWEPT_FACE",FACE,{"disambiguationData":[OSD([sQuery(id+"F30.wireOp",EDGE,"E34.top")])]})]});
            var Q1;
            Q1=makeQuery(id+"F31.boolean.opBoolean","INTERSECT",EDGE,{"derivedFrom":[makeQuery(id+"F9.boolean.opBoolean","MERGE",FACE,{"derivedFrom":[makeQuery(id+"F1.opExtrude","SWEPT_FACE",FACE,{"disambiguationData":[OSD([sQuery(id+"F0.wireOp",EDGE,"E13")])]}),makeQuery(id+"F9.opExtrude","CAP_FACE",FACE,{"disambiguationData":[OSD([sQuery(id+"F8.wireOp",EDGE,"E23"),sQuery(id+"F8.wireOp",EDGE,"E24"),sQuery(id+"F8.wireOp",EDGE,"E25"),sQuery(id+"F8.wireOp",EDGE,"E27")])],"isStart":true})]}),makeQuery(id+"F31.opExtrude","SWEPT_FACE",FACE,{"disambiguationData":[OSD([sQuery(id+"F30.wireOp",EDGE,"E34.bottom")])]})]});
            var Q2;
            Q2=makeQuery(id+"F31.boolean.opBoolean","INTERSECT",EDGE,{"derivedFrom":[makeQuery(id+"F10.boolean.opBoolean","MERGE",FACE,{"derivedFrom":[makeQuery(id+"F1.opExtrude","SWEPT_FACE",FACE,{"disambiguationData":[OSD([sQuery(id+"F0.wireOp",EDGE,"E12")])]}),makeQuery(id+"F10.opExtrude","CAP_FACE",FACE,{"disambiguationData":[OSD([sQuery(id+"F8.wireOp",EDGE,"E23"),sQuery(id+"F8.wireOp",EDGE,"E24"),sQuery(id+"F8.wireOp",EDGE,"E25"),sQuery(id+"F8.wireOp",EDGE,"E27")])],"isStart":true})]}),makeQuery(id+"F31.opExtrude","SWEPT_FACE",FACE,{"disambiguationData":[OSD([sQuery(id+"F30.wireOp",EDGE,"E34.top")])]})]});
            var Q3;
            Q3=makeQuery(id+"F31.boolean.opBoolean","COPY",EDGE,{"derivedFrom":makeQuery(id+"F31.opExtrude","CAP_EDGE",EDGE,{"disambiguationData":[OSD([sQuery(id+"F30.wireOp",EDGE,"E34.right")])],"isStart":true})});
            fillet(context, id + "F32", {"entities" : qUnion([Q0, Q1, Q2, Q3]), "radius" : 1 * mm, "tangentPropagation" : true, "allowEdgeOverflow" : false});
        }
        {
            var Q0;
            Q0=makeQuery(id+"F7.boolean.opBoolean","MERGE",FACE,{"derivedFrom":[makeQuery(id+"F1.opExtrude","SWEPT_FACE",FACE,{"disambiguationData":[OSD([sQuery(id+"F0.wireOp",EDGE,"E7")])]}),makeQuery(id+"F7.opExtrude","CAP_FACE",FACE,{"disambiguationData":[OSD([sQuery(id+"F0.wireOp",EDGE,"E5"),sQuery(id+"F0.wireOp",EDGE,"E6"),sQuery(id+"F6.wireOp",EDGE,"E22")])],"isStart":false})]});
            var sketch = newSketch(context, id + "F33", { "sketchPlane" : qUnion([Q0])});
            skLineSegment(sketch, "E39.bottom", {"start": v(23.94, 4.5) * mm, "end": v(49.94, 4.5) * mm});
            skLineSegment(sketch, "E39.top", {"start": v(23.94, -4.5) * mm, "end": v(49.94, -4.5) * mm});
            skLineSegment(sketch, "E39.left", {"start": v(21.94, 2.5) * mm, "end": v(21.94, -2.5) * mm});
            skLineSegment(sketch, "E39.right", {"start": v(51.94, 2.5) * mm, "end": v(51.94, -2.5) * mm});
            skPoint(sketch, "E40.visualSharp", {"position": v(21.94, 4.5) * mm});
            skArc(sketch, "E40.filletArc", {"start": v(23.94, 4.5) * mm, "mid": v(22.52, 3.91) * mm, "end": v(21.94, 2.5) * mm});
            skPoint(sketch, "E41.visualSharp", {"position": v(21.94, -4.5) * mm});
            skArc(sketch, "E41.filletArc", {"start": v(21.94, -2.5) * mm, "mid": v(22.52, -3.91) * mm, "end": v(23.94, -4.5) * mm});
            skPoint(sketch, "E42.visualSharp", {"position": v(51.94, 4.5) * mm});
            skArc(sketch, "E42.filletArc", {"start": v(51.94, 2.5) * mm, "mid": v(51.35, 3.91) * mm, "end": v(49.94, 4.5) * mm});
            skPoint(sketch, "E43.visualSharp", {"position": v(51.94, -4.5) * mm});
            skArc(sketch, "E43.filletArc", {"start": v(49.94, -4.5) * mm, "mid": v(51.35, -3.91) * mm, "end": v(51.94, -2.5) * mm});
            skSolve(sketch);
        }
        {
            var Q0;
            Q0 = qSketchRegion(id + "F33", true);
            extrude(context, id + "F34", {"entities" : qUnion([Q0]), "operationType" : NewBodyOperationType.REMOVE, "endBound" : BoundingType.THROUGH_ALL, "oppositeDirection" : true, "depth" : 25 * mm, "offsetDistance" : 25 * mm});
        }
        {
            var Q0;
            Q0=makeQuery(id+"F34.boolean.opBoolean","COPY",EDGE,{"derivedFrom":makeQuery(id+"F34.opExtrude","CAP_EDGE",EDGE,{"disambiguationData":[OSD([sQuery(id+"F33.wireOp",EDGE,"E39.bottom")])],"isStart":true})});
            var Q1;
            Q1=makeQuery(id+"F34.boolean.opBoolean","INTERSECT",EDGE,{"derivedFrom":[makeQuery(id+"F5.boolean.opBoolean","MERGE",FACE,{"derivedFrom":[makeQuery(id+"F1.opExtrude","SWEPT_FACE",FACE,{"disambiguationData":[OSD([sQuery(id+"F0.wireOp",EDGE,"E4")])]}),makeQuery(id+"F5.opExtrude","CAP_FACE",FACE,{"disambiguationData":[OSD([sQuery(id+"F4.wireOp",EDGE,"E21")])],"isStart":true})]}),makeQuery(id+"F34.opExtrude","SWEPT_FACE",FACE,{"disambiguationData":[OSD([sQuery(id+"F33.wireOp",EDGE,"E39.top")])]})]});
            var Q2;
            Q2=makeQuery(id+"F34.boolean.opBoolean","INTERSECT",EDGE,{"derivedFrom":[makeQuery(id+"F1.opExtrude","SWEPT_FACE",FACE,{"disambiguationData":[OSD([sQuery(id+"F0.wireOp",EDGE,"E1")])]}),makeQuery(id+"F34.opExtrude","SWEPT_FACE",FACE,{"disambiguationData":[OSD([sQuery(id+"F33.wireOp",EDGE,"E39.top")])]})]});
            var Q3;
            Q3=makeQuery(id+"F34.boolean.opBoolean","INTERSECT",EDGE,{"disambiguationData":[OD(0.0)],"derivedFrom":[makeQuery(id+"F1.opExtrude","SWEPT_FACE",FACE,{"disambiguationData":[OSD([sQuery(id+"F0.wireOp",EDGE,"E16")])]}),makeQuery(id+"F34.opExtrude","SWEPT_FACE",FACE,{"disambiguationData":[OSD([sQuery(id+"F33.wireOp",EDGE,"E39.top")])]})]});
            fillet(context, id + "F35", {"entities" : qUnion([Q0, Q1, Q2, Q3]), "radius" : 1 * mm, "tangentPropagation" : true, "allowEdgeOverflow" : false});
        }
    });
